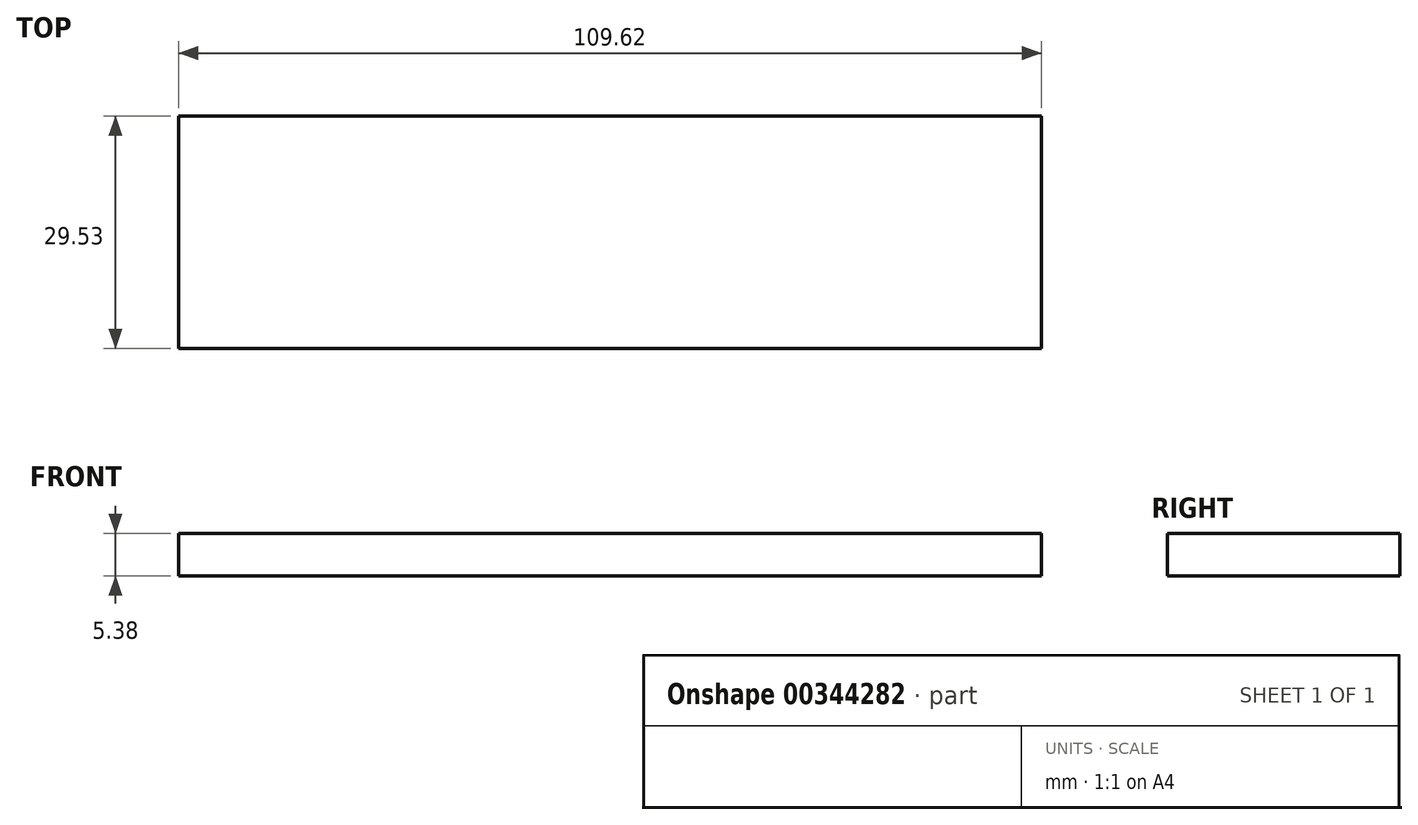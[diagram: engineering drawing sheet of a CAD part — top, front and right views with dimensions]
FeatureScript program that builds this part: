
annotation { "Feature Type Name" : "Feature", "Feature Type Description" : "" }
export const myFeature = defineFeature(function(context is Context, id is Id, definition is map)
    precondition{}
    {
        {
            var Q0;
            Q0=qCreatedBy(makeId("Front.planeOp"),FACE);
            var sketch = newSketch(context, id + "F0", { "sketchPlane" : qUnion([Q0])});
            skLineSegment(sketch, "E0.bottom", {"start": v(54.65, 52.31) * mm, "end": v(-54.97, 52.31) * mm});
            skLineSegment(sketch, "E0.top", {"start": v(54.65, 46.93) * mm, "end": v(-54.97, 46.93) * mm});
            skLineSegment(sketch, "E0.left", {"start": v(54.65, 52.31) * mm, "end": v(54.65, 46.93) * mm});
            skLineSegment(sketch, "E0.right", {"start": v(-54.97, 52.31) * mm, "end": v(-54.97, 46.93) * mm});
            skSolve(sketch);
        }
        {
            var Q0;
            Q0 = qSketchRegion(id + "F0", true);
            extrude(context, id + "F1", {"entities" : qUnion([Q0]), "depth" : 29.53 * mm});
        }
    });
